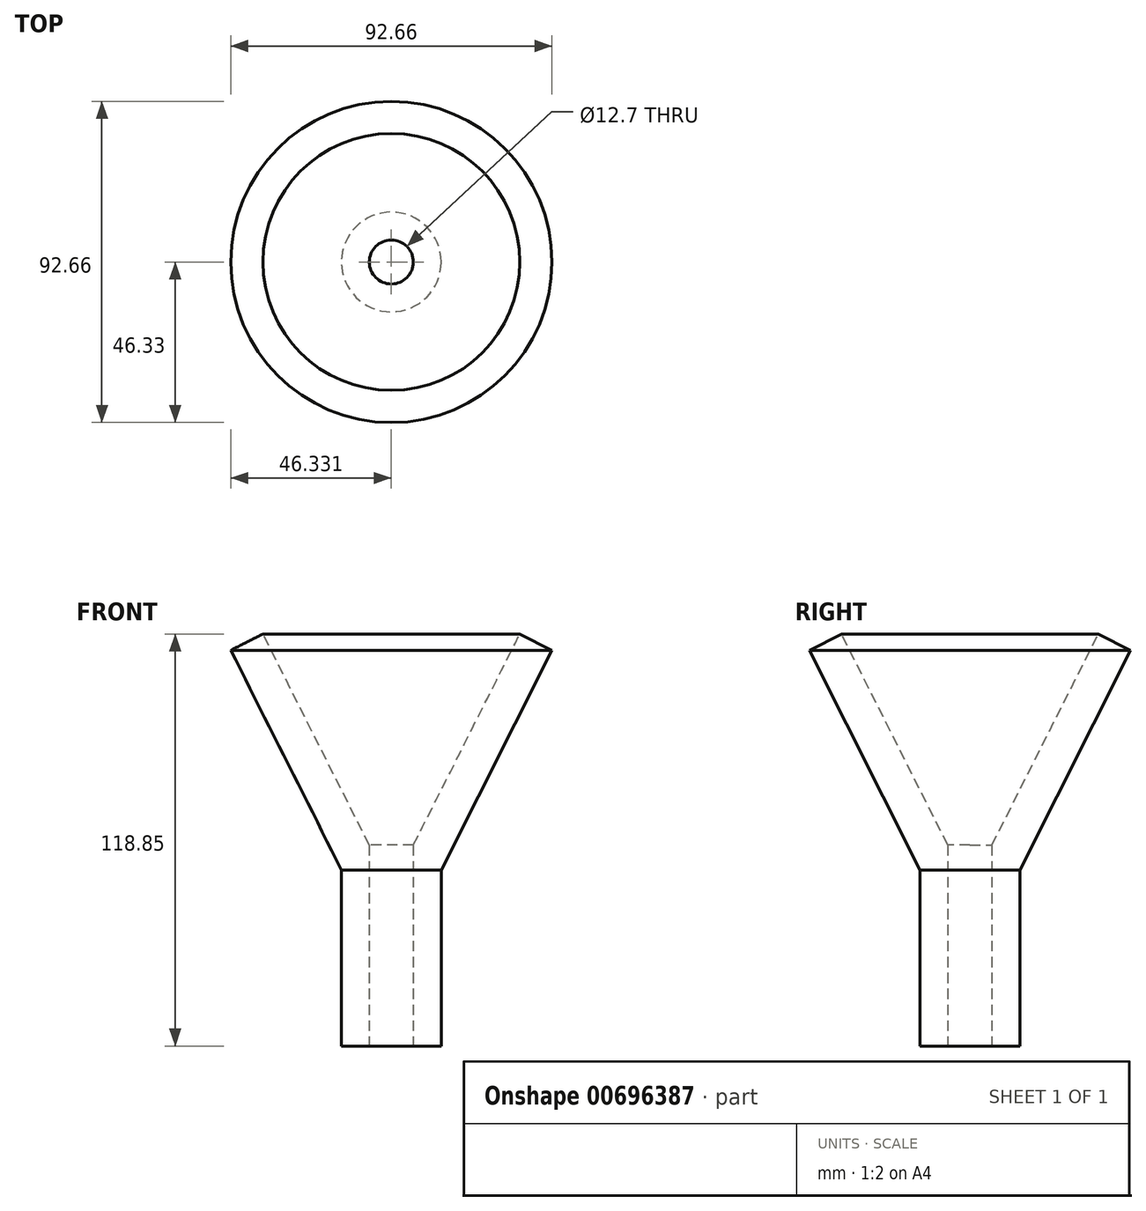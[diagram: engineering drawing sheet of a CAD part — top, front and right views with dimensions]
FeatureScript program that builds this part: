
annotation { "Feature Type Name" : "Feature", "Feature Type Description" : "" }
export const myFeature = defineFeature(function(context is Context, id is Id, definition is map)
    precondition{}
    {
        {
            var Q0;
            Q0=qCreatedBy(makeId("Front.planeOp"),FACE);
            var sketch = newSketch(context, id + "F0", { "sketchPlane" : qUnion([Q0])});
            skLineSegment(sketch, "E0", {"start": v(0, 0) * mm, "end": v(34.3, 68.05) * mm});
            skLineSegment(sketch, "E1", {"start": v(34.3, 68.05) * mm, "end": v(43.58, 63.37) * mm});
            skLineSegment(sketch, "E2", {"start": v(43.58, 63.37) * mm, "end": v(11.64, 0) * mm});
            skLineSegment(sketch, "E3", {"start": v(11.64, 0) * mm, "end": v(0, 0) * mm});
            skLineSegment(sketch, "E4", {"start": v(0, -50.8) * mm, "end": v(-2.75, -50.8) * mm});
            skLineSegment(sketch, "E5", {"start": v(-2.75, -50.8) * mm, "end": v(-2.75, 0) * mm});
            skLineSegment(sketch, "E6", {"start": v(-2.75, 0) * mm, "end": v(0, 0) * mm});
            skLineSegment(sketch, "E7", {"start": v(11.64, 0) * mm, "end": v(11.64, -50.8) * mm});
            skLineSegment(sketch, "E8", {"start": v(11.64, -50.8) * mm, "end": v(-2.75, -50.8) * mm});
            skSolve(sketch);
        }
        {
            var Q0;
            Q0=makeQuery(id+"F0.imprint","IMPRINT",FACE,{"disambiguationData":[TD([[makeQuery(id+"F0.imprint","IMPRINT",EDGE,{"derivedFrom":sQuery(id+"F0.wireOp",EDGE,"E3")}),1.0]])]});
            var Q1;
            Q1=makeQuery(id+"F0.imprint","IMPRINT",FACE,{"disambiguationData":[TD([[makeQuery(id+"F0.imprint","IMPRINT",EDGE,{"derivedFrom":sQuery(id+"F0.wireOp",EDGE,"E0")}),-1.0]])]});
            var Q2;
            Q2=sQuery(id+"F0.wireOp",EDGE,"E5");
            revolve(context, id + "F1", {"entities" : qUnion([Q0, Q1]), "axis" : qUnion([Q2]), "revolveType" : RevolveType.FULL});
        }
        {
            var Q0;
            Q0=makeQuery(id+"F1.opRevolve","SWEPT_FACE",FACE,{"disambiguationData":[OSD([sQuery(id+"F0.wireOp",EDGE,"E8")])]});
            var sketch = newSketch(context, id + "F2", { "sketchPlane" : qUnion([Q0])});
            skCircle(sketch, "E9", {"center": v(-2.75, 0) * mm, "radius": 6.35 * mm});
            skSolve(sketch);
        }
        {
            var Q0;
            Q0=makeQuery(id+"F2.imprint","IMPRINT",FACE,{"disambiguationData":[TD([[makeQuery(id+"F2.imprint","IMPRINT",EDGE,{"derivedFrom":sQuery(id+"F2.wireOp",EDGE,"E9")}),1.0]])]});
            extrude(context, id + "F3", {"entities" : qUnion([Q0]), "operationType" : NewBodyOperationType.REMOVE, "oppositeDirection" : true, "depth" : 72.64 * mm, "offsetDistance" : 25.4 * mm});
        }
    });
